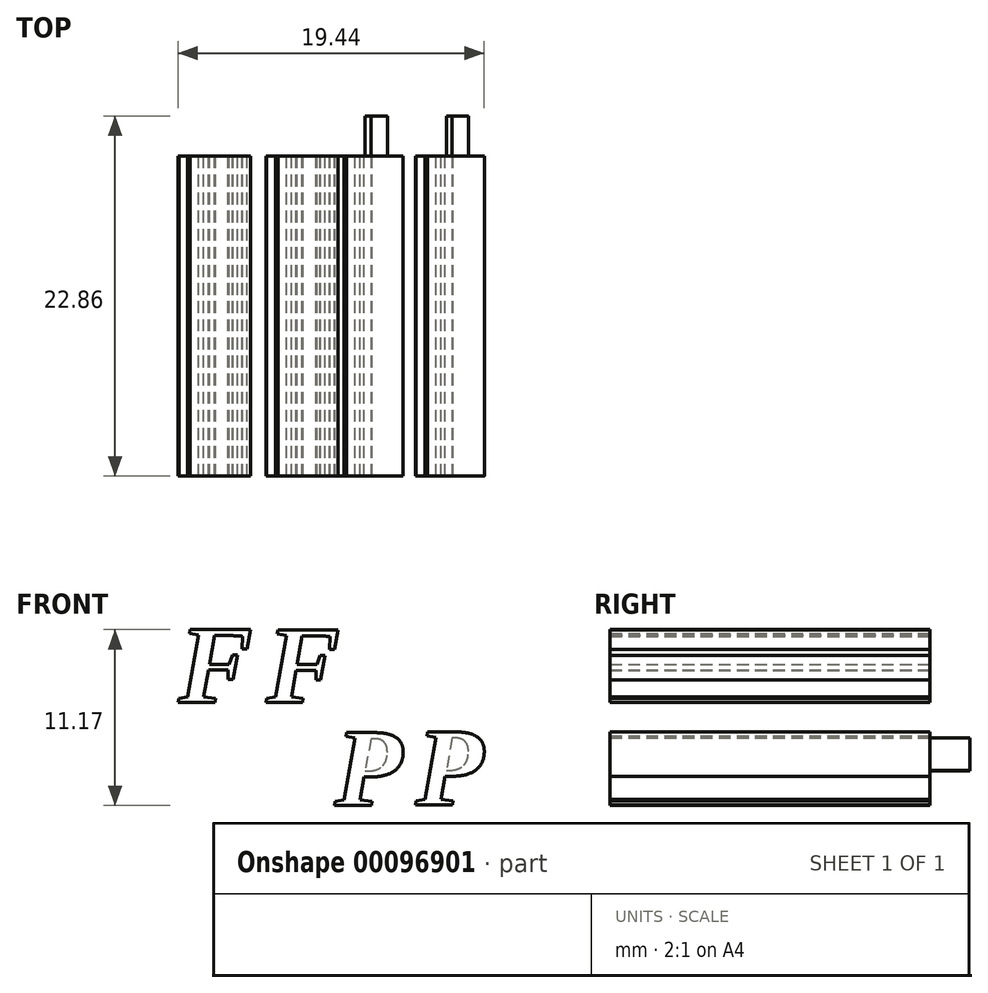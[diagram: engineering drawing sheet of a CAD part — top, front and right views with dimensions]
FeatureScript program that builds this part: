
annotation { "Feature Type Name" : "Feature", "Feature Type Description" : "" }
export const myFeature = defineFeature(function(context is Context, id is Id, definition is map)
    precondition{}
    {
        {
            var Q0;
            Q0=qCreatedBy(makeId("Front.planeOp"),FACE);
            var sketch = newSketch(context, id + "F0", { "sketchPlane" : qUnion([Q0])});
            skArc(sketch, "E0", {"start": v(-11.11, 0) * mm, "mid": v(-11.5, 11.57) * mm, "end": v(0, 10.16) * mm});
            skArc(sketch, "E1", {"start": v(0, 10.16) * mm, "mid": v(11.5, 11.57) * mm, "end": v(11.11, 0) * mm});
            skLineSegment(sketch, "E2", {"start": v(-11.11, 0) * mm, "end": v(0, -12.7) * mm});
            skLineSegment(sketch, "E3", {"start": v(0, -12.7) * mm, "end": v(11.11, 0) * mm});
            skLineSegment(sketch, "E4", {"start": v(-6.35, 5.95) * mm, "end": v(6.35, 5.95) * mm, "construction": true});
            skText(sketch, "E5", { "text": "F", "fontName": "Tinos-BoldItalic.ttf"});
            skPoint(sketch, "E6", {"position": v(-6.45, 6.5) * mm});
            skText(sketch, "E7", { "text": "F", "fontName": "Tinos-BoldItalic.ttf"});
            skText(sketch, "E8", { "text": "P", "fontName": "Tinos-BoldItalic.ttf"});
            skText(sketch, "E9", { "text": "P", "fontName": "Tinos-BoldItalic.ttf"});
            skPoint(sketch, "E10", {"position": v(-11.05, 6.5) * mm});
            skPoint(sketch, "E11", {"position": v(-5.48, 6.47) * mm});
            skPoint(sketch, "E12", {"position": v(-0.88, 6.47) * mm});
            skPoint(sketch, "E13", {"position": v(-1.12, -0.05) * mm});
            skPoint(sketch, "E14", {"position": v(3.24, -0.05) * mm});
            skPoint(sketch, "E15", {"position": v(4.03, -0.02) * mm});
            skPoint(sketch, "E16", {"position": v(8.39, -0.02) * mm});
            skLineSegment(sketch, "E17", {"start": v(-11.5, 11.57) * mm, "end": v(0, 0) * mm, "construction": true});
            skLineSegment(sketch, "E18", {"start": v(11.5, 11.57) * mm, "end": v(0, 0) * mm, "construction": true});
            const initialGuessF0  = {"E5": [-0.01105, 0.00395, 1, 0, 0.00508], "E7": [-0.00548, 0.00393, 1, 0, 0.00508], "E8": [0.00403, -0.00256, 1, 0, 0.00508], "E9": [-0.00112, -0.0026, 1, 0, 0.00508]};
            skSetInitialGuess(sketch, initialGuessF0);
            skSolve(sketch);
        }
        {
            var Q0;
            Q0=makeQuery(id+"F0.imprint","IMPRINT",FACE,{"disambiguationData":[TD([[makeQuery(id+"F0.imprint","IMPRINT",EDGE,{"derivedFrom":sQuery(id+"F0.wireOp",EDGE,"E0")}),-1.0]])]});
            var Q1;
            Q1=makeQuery(id+"F0.imprint","IMPRINT",FACE,{"disambiguationData":[TD([[makeQuery(id+"F0.imprint","IMPRINT",EDGE,{"derivedFrom":sQuery(id+"F0.wireOp",EDGE,"E5.sketch_text.stroke-0")}),-1.0]])]});
            var Q2;
            Q2=makeQuery(id+"F0.imprint","IMPRINT",FACE,{"disambiguationData":[TD([[makeQuery(id+"F0.imprint","IMPRINT",EDGE,{"derivedFrom":sQuery(id+"F0.wireOp",EDGE,"E7.sketch_text.stroke-0")}),-1.0]])]});
            var Q3;
            Q3=makeQuery(id+"F0.imprint","IMPRINT",FACE,{"disambiguationData":[TD([[makeQuery(id+"F0.imprint","IMPRINT",EDGE,{"derivedFrom":sQuery(id+"F0.wireOp",EDGE,"E9.sketch_text.stroke-0")}),-1.0]])]});
            var Q4;
            Q4=makeQuery(id+"F0.imprint","IMPRINT",FACE,{"disambiguationData":[TD([[makeQuery(id+"F0.imprint","IMPRINT",EDGE,{"derivedFrom":sQuery(id+"F0.wireOp",EDGE,"E9.sketch_text.stroke-0")}),1.0]])]});
            var Q5;
            Q5=makeQuery(id+"F0.imprint","IMPRINT",FACE,{"disambiguationData":[TD([[makeQuery(id+"F0.imprint","IMPRINT",EDGE,{"derivedFrom":sQuery(id+"F0.wireOp",EDGE,"E8.sketch_text.stroke-0")}),1.0]])]});
            var Q6;
            Q6=makeQuery(id+"F0.imprint","IMPRINT",FACE,{"disambiguationData":[TD([[makeQuery(id+"F0.imprint","IMPRINT",EDGE,{"derivedFrom":sQuery(id+"F0.wireOp",EDGE,"E8.sketch_text.stroke-0")}),-1.0]])]});
            extrude(context, id + "F1", {"entities" : qUnion([Q0, Q1, Q2, Q3, Q4, Q5, Q6]), "depth" : 20.32 * mm});
        }
        {
            var Q0;
            Q0=makeQuery(id+"F0.imprint","IMPRINT",FACE,{"disambiguationData":[TD([[makeQuery(id+"F0.imprint","IMPRINT",EDGE,{"derivedFrom":sQuery(id+"F0.wireOp",EDGE,"E0")}),-1.0]])]});
            var Q1;
            Q1=makeQuery(id+"F0.imprint","IMPRINT",FACE,{"disambiguationData":[TD([[makeQuery(id+"F0.imprint","IMPRINT",EDGE,{"derivedFrom":sQuery(id+"F0.wireOp",EDGE,"E9.sketch_text.stroke-0")}),1.0]])]});
            var Q2;
            Q2=makeQuery(id+"F0.imprint","IMPRINT",FACE,{"disambiguationData":[TD([[makeQuery(id+"F0.imprint","IMPRINT",EDGE,{"derivedFrom":sQuery(id+"F0.wireOp",EDGE,"E8.sketch_text.stroke-0")}),1.0]])]});
            extrude(context, id + "F2", {"entities" : qUnion([Q0, Q1, Q2]), "operationType" : NewBodyOperationType.ADD, "oppositeDirection" : true, "depth" : 2.54 * mm});
        }
    });
